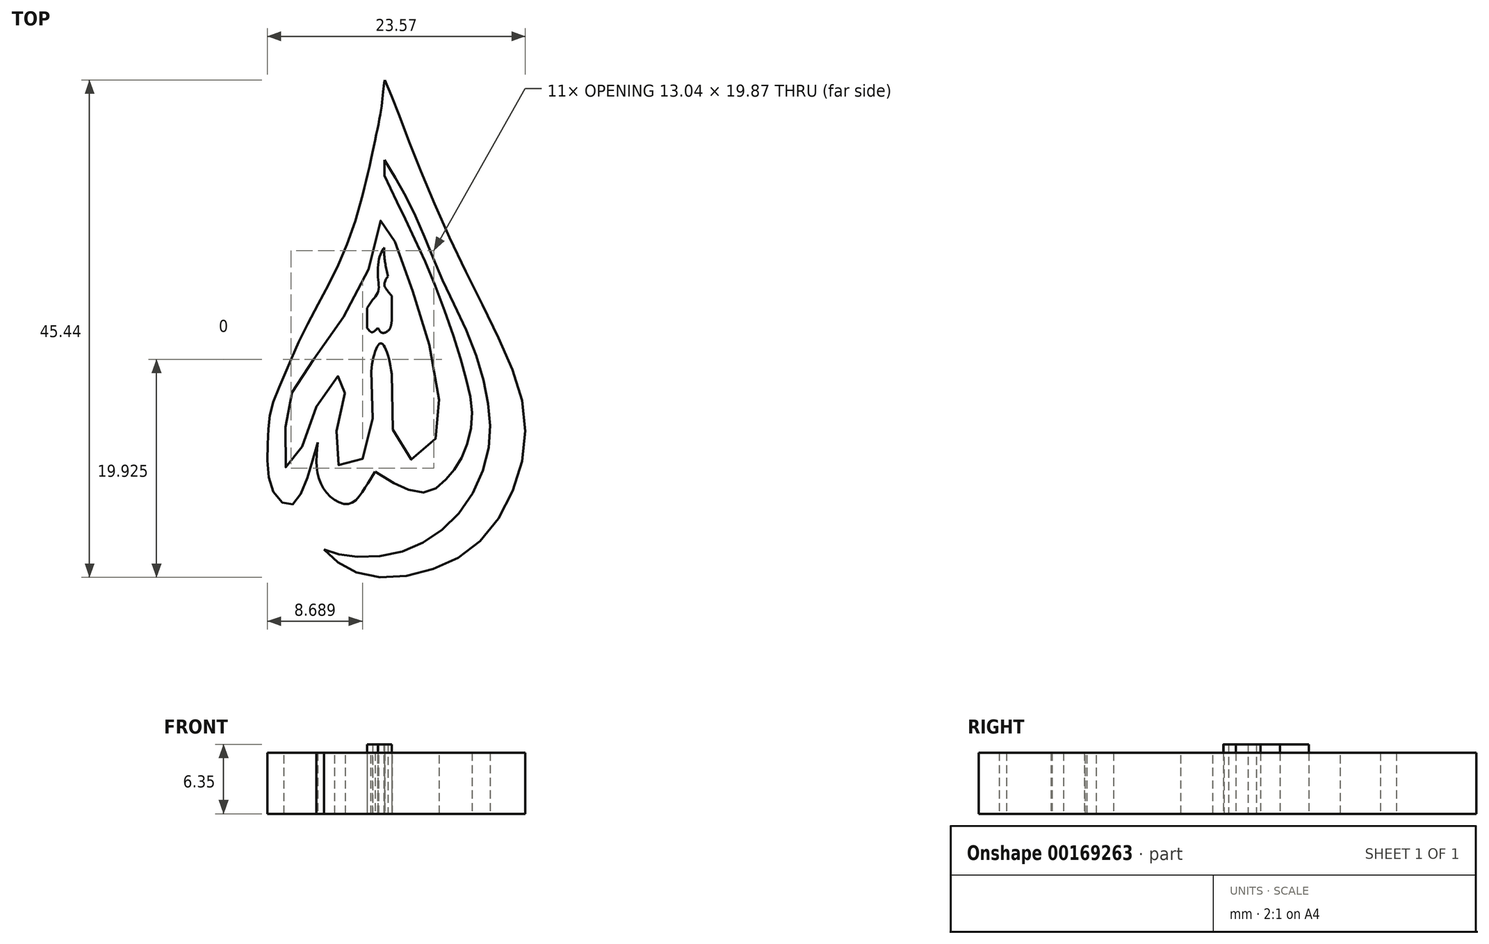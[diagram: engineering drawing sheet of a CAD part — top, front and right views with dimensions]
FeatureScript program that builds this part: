
annotation { "Feature Type Name" : "Feature", "Feature Type Description" : "" }
export const myFeature = defineFeature(function(context is Context, id is Id, definition is map)
    precondition{}
    {
        {
            var Q0;
            Q0=qCreatedBy(makeId("Top.planeOp"),FACE);
            var sketch = newSketch(context, id + "F0", { "sketchPlane" : qUnion([Q0])});
            skFitSpline(sketch, "E0", {"points": [v(-3.07, 12.85) * mm, v(-3.29, 11.18) * mm, v(-3.92, 7.57) * mm, v(-5.96, -0.6) * mm, v(-8.43, -6.23) * mm, v(-10.99, -11.16) * mm, v(-12.26, -14.14) * mm, v(-13.37, -16.87) * mm, v(-13.71, -19.08) * mm, v(-13.8, -22.15) * mm, v(-13.11, -25.04) * mm, v(-11.67, -25.98) * mm, v(-10.39, -24.1) * mm, v(-9.2, -20.27) * mm], "startDerivative": vector(-9.02, -28.13) * mm, "endDerivative": vector(13.39, 47.7) * mm});
            skFitSpline(sketch, "E1", {"points": [v(-9.2, -20.27) * mm, v(-9.2, -23.22) * mm, v(-7.97, -25.28) * mm, v(-6.25, -25.85) * mm, v(-4.96, -24.51) * mm, v(-3.96, -22.93) * mm], "startDerivative": vector(-1.31, -13.09) * mm, "endDerivative": vector(5.18, 8.17) * mm});
            skFitSpline(sketch, "E2", {"points": [v(-3.96, -22.93) * mm, v(-2.71, -23.7) * mm, v(0.4, -24.85) * mm, v(2.5, -23.65) * mm, v(3.98, -21.59) * mm, v(4.88, -18.2) * mm, v(4.31, -14.29) * mm, v(1.54, -5.97) * mm, v(-1.71, 1.2) * mm, v(-3.1, 4.11) * mm], "startDerivative": vector(15.2, -9.73) * mm, "endDerivative": vector(-12.06, 25.58) * mm});
            skLineSegment(sketch, "E3", {"start": v(-3.1, 4.11) * mm, "end": v(-3.1, 5.55) * mm});
            skFitSpline(sketch, "E4", {"points": [v(-3.1, 5.55) * mm, v(-1.23, 2.4) * mm, v(0.54, -1.43) * mm, v(2.35, -5.73) * mm, v(5.03, -11.6) * mm, v(6.37, -16.72) * mm, v(6.41, -20.78) * mm, v(4.7, -25.37) * mm, v(1.44, -28.76) * mm, v(-2.47, -30.48) * mm, v(-6.49, -30.63) * mm, v(-8.64, -30.05) * mm], "startDerivative": vector(22.84, -36.58) * mm, "endDerivative": vector(-30.02, 10.38) * mm});
            skFitSpline(sketch, "E5", {"points": [v(-8.64, -30.05) * mm, v(-6.68, -31.68) * mm, v(-3.1, -32.59) * mm, v(1.87, -31.63) * mm, v(6.08, -28.81) * mm, v(9.14, -23.22) * mm, v(9.57, -16.96) * mm, v(6.84, -9.75) * mm, v(2.69, -1.2) * mm, v(-0.56, 6.5) * mm, v(-2.28, 10.94) * mm, v(-3.07, 12.85) * mm], "startDerivative": vector(27.9, -28.13) * mm, "endDerivative": vector(-12.92, 30.6) * mm});
            skFitSpline(sketch, "E6", {"points": [v(-3.22, 0.46) * mm, v(-3.89, -2.26) * mm, v(-6.04, -7.42) * mm, v(-9.14, -12.1) * mm, v(-11.25, -14.97) * mm, v(-11.92, -17.27) * mm, v(-12.25, -20.18) * mm, v(-12.01, -22.67) * mm, v(-11.2, -21.9) * mm, v(-9.86, -18.41) * mm, v(-8.67, -15.69) * mm, v(-7.1, -14.11) * mm, v(-6.7, -14.62) * mm, v(-6.8, -16.12) * mm, v(-7.48, -19.2) * mm, v(-7.52, -21.7) * mm, v(-6.66, -22.86) * mm, v(-4.94, -21.52) * mm, v(-4.18, -18.13) * mm, v(-4.32, -13.78) * mm, v(-3.46, -11.2) * mm, v(-2.45, -14.02) * mm, v(-2.22, -19.85) * mm, v(-0.83, -21.8) * mm, v(0.94, -21.04) * mm, v(1.85, -18.56) * mm, v(1.7, -14.83) * mm, v(0.03, -7.95) * mm, v(-1.7, -3.31) * mm, v(-3.22, 0.46) * mm]});
            skLineSegment(sketch, "E7", {"start": v(-4.2, -7.22) * mm, "end": v(-4.7, -7.98) * mm});
            skLineSegment(sketch, "E8", {"start": v(-2.45, -6.87) * mm, "end": v(-2.45, -9.12) * mm});
            skLineSegment(sketch, "E9", {"start": v(-4.7, -7.98) * mm, "end": v(-4.7, -9.78) * mm});
            skFitSpline(sketch, "E10", {"points": [v(-4.7, -9.78) * mm, v(-4.25, -10.19) * mm, v(-3.7, -9.78) * mm], "startDerivative": vector(0.88, -1.24) * mm, "endDerivative": vector(1.12, 1.2) * mm});
            skFitSpline(sketch, "E11", {"points": [v(-3.7, -9.78) * mm, v(-3.32, -10.24) * mm, v(-2.69, -9.96) * mm, v(-2.45, -9.12) * mm], "startDerivative": vector(1, -2.02) * mm, "endDerivative": vector(0.24, 2.5) * mm});
            skLineSegment(sketch, "E12", {"start": v(-4.25, -10.19) * mm, "end": v(-4.32, -13.78) * mm});
            skLineSegment(sketch, "E13", {"start": v(-2.69, -9.96) * mm, "end": v(-2.45, -14.02) * mm});
            skFitSpline(sketch, "E14", {"points": [v(-4.2, -7.22) * mm, v(-3.67, -6.46) * mm, v(-3.7, -5.2) * mm, v(-3.54, -3.27) * mm, v(-3.12, -2.44) * mm], "startDerivative": vector(3, 3.3) * mm, "endDerivative": vector(2.2, 3.23) * mm});
            skFitSpline(sketch, "E15", {"points": [v(-3.12, -2.44) * mm, v(-3.12, -3.32) * mm, v(-2.8, -5.07) * mm], "startDerivative": vector(-0.11, -1.95) * mm, "endDerivative": vector(0.7, -3.24) * mm});
            skFitSpline(sketch, "E16", {"points": [v(-2.8, -5.07) * mm, v(-3.12, -5.82) * mm, v(-2.8, -6.44) * mm, v(-2.45, -6.87) * mm], "startDerivative": vector(-1.38, -2.07) * mm, "endDerivative": vector(1.12, -1.33) * mm});
            skCircle(sketch, "E17", {"center": v(-6.72, 8.65) * mm, "radius": 1.59 * mm});
            skArc(sketch, "E18", {"start": v(-3.07, 12.85) * mm, "mid": v(-11.9, 9.12) * mm, "end": v(-5.1, 2.35) * mm});
            skSolve(sketch);
        }
        {
            var Q0;
            {var subQ9=sQuery(id+"F0.wireOp",EDGE,"E1");Q0=makeQuery(id+"F0.imprint","IMPRINT",FACE,{"disambiguationData":[TD([[makeQuery(id+"F0.imprint","IMPRINT",EDGE,{"derivedFrom":subQ9}),1.0]])]});}
            var Q1;
            Q1=makeQuery(id+"F0.imprint","IMPRINT",FACE,{"disambiguationData":[TD([[makeQuery(id+"F0.imprint","IMPRINT",EDGE,{"derivedFrom":sQuery(id+"F0.wireOp",EDGE,"u4uKVAOh-BXcH-bhgs-RwS0-NUXnGsfmfyaU")}),-1.0]])]});
            extrude(context, id + "F1", {"entities" : qUnion([Q0, Q1]), "depth" : 5.6 * mm});
        }
        {
            var Q0;
            Q0=makeQuery(id+"F0.imprint","IMPRINT",FACE,{"disambiguationData":[TD([[makeQuery(id+"F0.imprint","IMPRINT",EDGE,{"derivedFrom":sQuery(id+"F0.wireOp",EDGE,"E7")}),1.0]])]});
            extrude(context, id + "F2", {"entities" : qUnion([Q0]), "operationType" : NewBodyOperationType.ADD, "depth" : 6.35 * mm});
        }
    });
